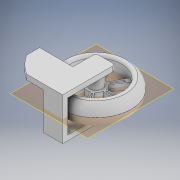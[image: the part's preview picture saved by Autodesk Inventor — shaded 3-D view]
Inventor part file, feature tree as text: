
AUTODESK INVENTOR PART (.ipt)
format: ipt  version: 2020 (Build 240168000, 168)  size: 338,944 bytes
history: native  units: mm
features: sketch x6, extrude x6, fillet x3, plane x1, mirror x1
ambient origin geometry x8: Origin, YZ Plane, XZ Plane, XY Plane, X Axis, Y Axis, Z Axis, Center Point
bodies: Solid1 (feature_tree)
feature tree (17):
  sketch  "Sketch1"  dims[d0=27.5mm d1=2.0mm]
  extrude  "Extrusion1"  Depth=2.0mm
  extrude  "Extrusion2"  Depth=5.0mm TaperAngle=360.0deg
  fillet  "Fillet1"  Radius=4.5mm
  sketch  "Sketch5"  dims[d18=6.0mm d19=60.0mm d21=360.0deg]
  fillet  "Fillet2"  Radius=5.0mm
  extrude  "Extrusion3"  Depth=60.0mm TaperAngle=360.0deg
  extrude  "Extrusion4"  Depth=10.0mm TaperAngle=0.0deg
  fillet  "Fillet3"  Radius=5.2mm
  extrude  "Extrusion5"  Depth=2.5mm
  plane  "Work Plane1"
  mirror  "Mirror1"
  extrude  "Extrusion6"  Depth=5.0mm TaperAngle=0.0deg
  sketch  "Sketch4"  dims[d8=0.5mm d9=0.5mm d10=60.0mm d12=360.0deg d14=4.5mm d17=5.0mm]
  sketch  "Sketch6"  dims[d23=2.5mm d24=0.0mm d25=10.0mm d26=0.0mm d27=5.2mm]
  sketch  "Sketch7"  dims[d28=7.0mm d29=2.5mm]
  sketch  "Sketch8"  dims[d30=1.0mm d31=5.0mm d32=0.0mm d33=7.5mm d34=7.5mm d35=11.0mm d36=7.5mm d37=2.0mm d38=2.0mm d39=0.0mm d40=1.0mm d41=2.0mm d42=6.26mm d43=0.0mm d44=9.0mm d45=13.0mm d46=2.5mm d47=5.0mm d48=2.0mm d49=0.0mm d15=0.5mm d16=0.872665mm d50=0.5mm d51=0.872665mm]
